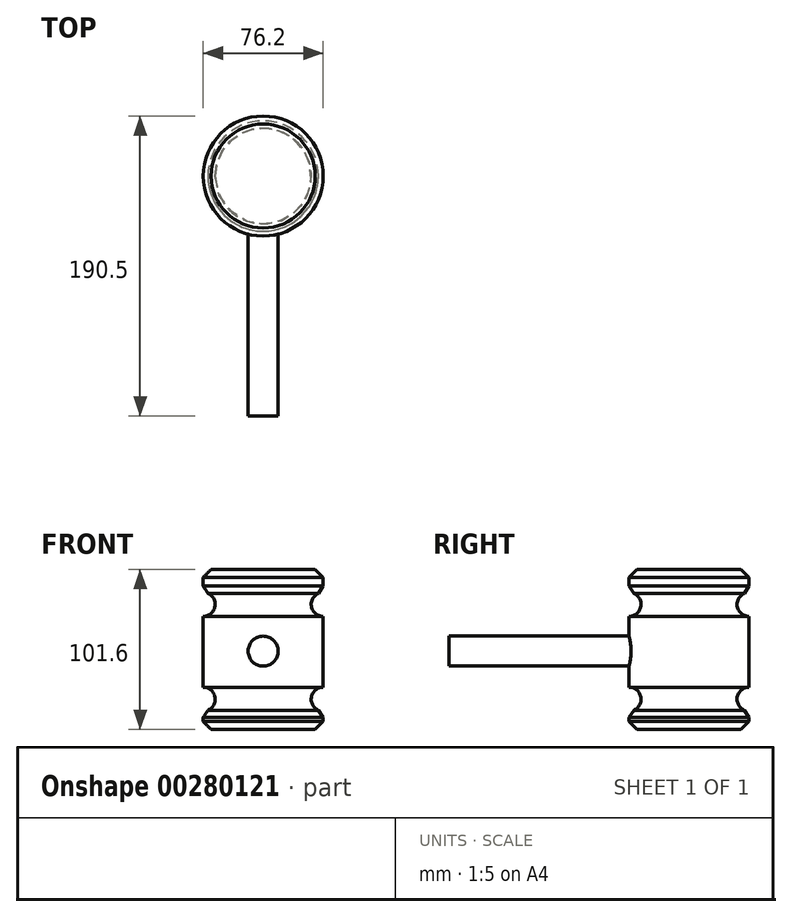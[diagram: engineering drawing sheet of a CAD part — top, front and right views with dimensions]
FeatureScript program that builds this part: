
annotation { "Feature Type Name" : "Feature", "Feature Type Description" : "" }
export const myFeature = defineFeature(function(context is Context, id is Id, definition is map)
    precondition{}
    {
        {
            var Q0;
            Q0=qCreatedBy(makeId("Front.planeOp"),FACE);
            var sketch = newSketch(context, id + "F0", { "sketchPlane" : qUnion([Q0])});
            skLineSegment(sketch, "E0.bottom", {"start": v(0, 0) * mm, "end": v(-38.1, 0) * mm});
            skLineSegment(sketch, "E0.top", {"start": v(0, 101.6) * mm, "end": v(-38.1, 101.6) * mm});
            skLineSegment(sketch, "E0.left", {"start": v(0, 0) * mm, "end": v(0, 101.6) * mm});
            skLineSegment(sketch, "E0.right", {"start": v(-38.1, 0) * mm, "end": v(-38.1, 11.6) * mm});
            skArc(sketch, "E1", {"start": v(-38.1, 71.82) * mm, "mid": v(-30.48, 79.44) * mm, "end": v(-38.1, 87.06) * mm});
            skArc(sketch, "E2", {"start": v(-38.1, 11.6) * mm, "mid": v(-30.48, 19.22) * mm, "end": v(-38.1, 26.84) * mm});
            skLineSegment(sketch, "E3.trimOffspring", {"start": v(-38.1, 26.84) * mm, "end": v(-38.1, 71.82) * mm});
            skLineSegment(sketch, "E4.trimOffspring", {"start": v(-38.1, 87.06) * mm, "end": v(-38.1, 101.6) * mm});
            skSolve(sketch);
        }
        {
            var Q0;
            Q0 = qSketchRegion(id + "F0", true);
            var Q1;
            Q1=sQuery(id+"F0.wireOp",EDGE,"E0.left");
            revolve(context, id + "F1", {"entities" : qUnion([Q0]), "axis" : qUnion([Q1]), "revolveType" : RevolveType.FULL});
        }
        {
            var Q0;
            Q0=qCreatedBy(makeId("Front.planeOp"),FACE);
            var sketch = newSketch(context, id + "F2", { "sketchPlane" : qUnion([Q0])});
            skCircle(sketch, "E5", {"center": v(0, 49.73) * mm, "radius": 9.53 * mm});
            skSolve(sketch);
        }
        {
            var Q0;
            Q0 = qSketchRegion(id + "F2", true);
            extrude(context, id + "F3", {"entities" : qUnion([Q0]), "operationType" : NewBodyOperationType.ADD, "depth" : 152.4 * mm});
        }
        {
            var Q0;
            Q0=makeQuery(id+"F1.opRevolve","SWEPT_FACE",FACE,{"disambiguationData":[OSD([sQuery(id+"F0.wireOp",EDGE,"E4.trimOffspring")])]});
            var Q1;
            Q1=makeQuery(id+"F1.opRevolve","SWEPT_FACE",FACE,{"disambiguationData":[OSD([sQuery(id+"F0.wireOp",EDGE,"E0.right")])]});
            chamfer(context, id + "F4", {"entities" : qUnion([Q0, Q1]), "width" : 5.08 * mm, "tangentPropagation" : true});
        }
    });
